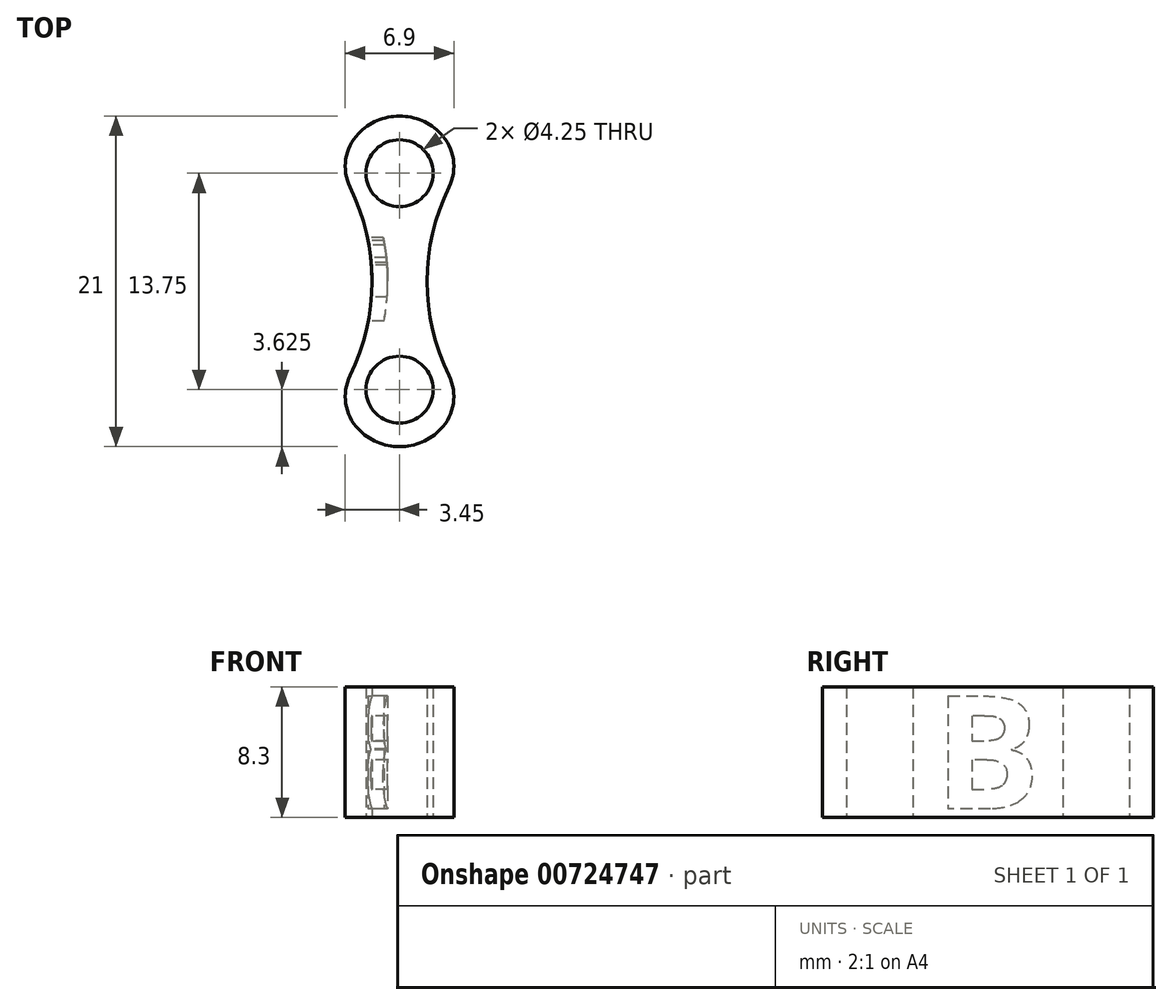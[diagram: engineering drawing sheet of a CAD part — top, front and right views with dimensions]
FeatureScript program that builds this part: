
annotation { "Feature Type Name" : "Feature", "Feature Type Description" : "" }
export const myFeature = defineFeature(function(context is Context, id is Id, definition is map)
    precondition{}
    {
        {
            var Q0;
            Q0=qCreatedBy(makeId("Top.planeOp"),FACE);
            var sketch = newSketch(context, id + "F0", { "sketchPlane" : qUnion([Q0])});
            skLineSegment(sketch, "E0", {"start": v(0, 6.88) * mm, "end": v(0, -6.88) * mm});
            skCircle(sketch, "E1", {"center": v(0, 6.88) * mm, "radius": 2.12 * mm});
            skLineSegment(sketch, "E2", {"start": v(-1.75, 0) * mm, "end": v(1.75, 0) * mm});
            skCircle(sketch, "E3", {"center": v(0, -6.88) * mm, "radius": 2.12 * mm});
            skCircle(sketch, "E4", {"center": v(0, 6.88) * mm, "radius": 3.62 * mm});
            skCircle(sketch, "E5", {"center": v(0, -6.88) * mm, "radius": 3.62 * mm});
            skArc(sketch, "E6", {"start": v(-3.12, -5.03) * mm, "mid": v(-1.75, 0) * mm, "end": v(-3.12, 5.03) * mm});
            skArc(sketch, "E7.MirrorCS", {"start": v(3.12, -5.03) * mm, "mid": v(1.75, 0) * mm, "end": v(3.12, 5.03) * mm});
            skPoint(sketch, "E8.orphan", {"position": v(3.12, 5.03) * mm});
            skPoint(sketch, "E9.orphan", {"position": v(-3.12, 5.03) * mm});
            skPoint(sketch, "E10.orphan", {"position": v(6.24, 6.88) * mm});
            skArc(sketch, "E11", {"start": v(-3.63, -6.87) * mm, "mid": v(-1.75, 0) * mm, "end": v(-3.63, 6.87) * mm});
            skArc(sketch, "E12.MirrorCS", {"start": v(3.63, -6.87) * mm, "mid": v(1.75, 0) * mm, "end": v(3.63, 6.87) * mm});
            skSolve(sketch);
        }
        {
            var Q0;
            Q0=makeQuery(id+"F0.imprint","IMPRINT",FACE,{"disambiguationData":[TD([[makeQuery(id+"F0.imprint","IMPRINT",EDGE,{"derivedFrom":sQuery(id+"F0.wireOp",EDGE,"E1")}),-1.0]])]});
            var Q1;
            {var subQ0=sQuery(id+"F0.wireOp",EDGE,"E4");var subQ1=sQuery(id+"F0.wireOp",EDGE,"E0");var subQ2=makeQuery(id+"F0.imprint","INTERSECT",VERTEX,{"derivedFrom":[subQ1,subQ0]});Q1=makeQuery(id+"F0.imprint","IMPRINT",FACE,{"disambiguationData":[TD([[makeQuery(id+"F0.imprint","IMPRINT",EDGE,{"disambiguationData":[TD([[subQ2,-1.0]])],"derivedFrom":subQ1}),-1.0]])]});}
            var Q2;
            {var subQ0=sQuery(id+"F0.wireOp",EDGE,"E4");var subQ1=sQuery(id+"F0.wireOp",EDGE,"E0");var subQ2=makeQuery(id+"F0.imprint","INTERSECT",VERTEX,{"derivedFrom":[subQ1,subQ0]});Q2=makeQuery(id+"F0.imprint","IMPRINT",FACE,{"disambiguationData":[TD([[makeQuery(id+"F0.imprint","IMPRINT",EDGE,{"disambiguationData":[TD([[subQ2,-1.0]])],"derivedFrom":subQ1}),1.0]])]});}
            var Q3;
            {var subQ0=sQuery(id+"F0.wireOp",EDGE,"E5");var subQ1=sQuery(id+"F0.wireOp",EDGE,"E0");var subQ2=makeQuery(id+"F0.imprint","INTERSECT",VERTEX,{"derivedFrom":[subQ1,subQ0]});Q3=makeQuery(id+"F0.imprint","IMPRINT",FACE,{"disambiguationData":[TD([[makeQuery(id+"F0.imprint","IMPRINT",EDGE,{"disambiguationData":[TD([[subQ2,1.0]])],"derivedFrom":subQ1}),1.0]])]});}
            var Q4;
            {var subQ0=sQuery(id+"F0.wireOp",EDGE,"E5");var subQ1=sQuery(id+"F0.wireOp",EDGE,"E0");var subQ2=makeQuery(id+"F0.imprint","INTERSECT",VERTEX,{"derivedFrom":[subQ1,subQ0]});Q4=makeQuery(id+"F0.imprint","IMPRINT",FACE,{"disambiguationData":[TD([[makeQuery(id+"F0.imprint","IMPRINT",EDGE,{"disambiguationData":[TD([[subQ2,1.0]])],"derivedFrom":subQ1}),-1.0]])]});}
            var Q5;
            Q5=makeQuery(id+"F0.imprint","IMPRINT",FACE,{"disambiguationData":[TD([[makeQuery(id+"F0.imprint","IMPRINT",EDGE,{"derivedFrom":sQuery(id+"F0.wireOp",EDGE,"E3")}),-1.0]])]});
            extrude(context, id + "F1", {"entities" : qUnion([Q0, Q1, Q2, Q3, Q4, Q5]), "depth" : 8.3 * mm, "offsetDistance" : 25 * mm});
        }
        {
            var Q0;
            Q0=makeQuery(id+"F1.opExtrude","CAP_VERTEX",VERTEX,{"disambiguationData":[OSD([sQuery(id+"F0.wireOp",EDGE,"E4"),sQuery(id+"F0.wireOp",EDGE,"E11")])],"isStart":false});
            var Q1;
            Q1=makeQuery(id+"F1.opExtrude","CAP_VERTEX",VERTEX,{"disambiguationData":[OSD([sQuery(id+"F0.wireOp",EDGE,"E4"),sQuery(id+"F0.wireOp",EDGE,"E11")])],"isStart":true});
            var Q2;
            Q2=makeQuery(id+"F1.opExtrude","CAP_VERTEX",VERTEX,{"disambiguationData":[OSD([sQuery(id+"F0.wireOp",EDGE,"E5"),sQuery(id+"F0.wireOp",EDGE,"E11")])],"isStart":true});
            cPlane(context, id + "F2", {"entities" : qUnion([Q0, Q1, Q2]), "cplaneType" : CPlaneType.THREE_POINT, "offset" : 10 * mm, "width" : 150 * mm, "height" : 150 * mm});
        }
        {
            var Q0;
            Q0=qCreatedBy(id+"F2.planeOp",FACE);
            var sketch = newSketch(context, id + "F3", { "sketchPlane" : qUnion([Q0])});
            skLineSegment(sketch, "E13", {"start": v(-1.85, 4.15) * mm, "end": v(1.85, 4.15) * mm});
            skPoint(sketch, "E14", {"position": v(0, 4.15) * mm});
            skSolve(sketch);
        }
        {
            var Q0;
            Q0=qCreatedBy(id+"F2.planeOp",FACE);
            var sketch = newSketch(context, id + "F4", { "sketchPlane" : qUnion([Q0])});
            skText(sketch, "E15", { "text": "B", "fontName": "OpenSans-Bold.ttf"});
            const initialGuessF4  = {"E15": [-0.00343, 0.00054, 1, 0, 0.00723]};
            skSetInitialGuess(sketch, initialGuessF4);
            skSolve(sketch);
        }
        {
            var Q0;
            Q0=makeQuery(id+"F4.imprint","IMPRINT",FACE,{"disambiguationData":[TD([[makeQuery(id+"F4.imprint","IMPRINT",EDGE,{"derivedFrom":sQuery(id+"F4.wireOp",EDGE,"E15.sketch_text.stroke-0")}),-1.0]])]});
            var Q1;
            Q1=makeQuery(id+"F1.opExtrude","SWEPT_FACE",FACE,{"disambiguationData":[OSD([sQuery(id+"F0.wireOp",EDGE,"E11")])]});
            extrude(context, id + "F5", {"entities" : qUnion([Q0]), "operationType" : NewBodyOperationType.REMOVE, "endBound" : BoundingType.UP_TO_SURFACE, "depth" : 25 * mm, "endBoundEntityFace" : qUnion([Q1]), "hasOffset" : true, "offsetDistance" : 1 * mm, "offsetOppositeDirection" : true});
        }
        {
            var Q0;
            Q0=makeQuery(id+"F1.opExtrude","SWEPT_EDGE",EDGE,{"disambiguationData":[OSD([sQuery(id+"F0.wireOp",EDGE,"E4"),sQuery(id+"F0.wireOp",EDGE,"E11")])]});
            var Q1;
            Q1=makeQuery(id+"F1.opExtrude","SWEPT_EDGE",EDGE,{"disambiguationData":[OSD([sQuery(id+"F0.wireOp",EDGE,"E5"),sQuery(id+"F0.wireOp",EDGE,"E11")])]});
            var Q2;
            Q2=makeQuery(id+"F1.opExtrude","SWEPT_EDGE",EDGE,{"disambiguationData":[OSD([sQuery(id+"F0.wireOp",EDGE,"E5"),sQuery(id+"F0.wireOp",EDGE,"E12.MirrorCS")])]});
            var Q3;
            Q3=makeQuery(id+"F1.opExtrude","SWEPT_EDGE",EDGE,{"disambiguationData":[OSD([sQuery(id+"F0.wireOp",EDGE,"E4"),sQuery(id+"F0.wireOp",EDGE,"E12.MirrorCS")])]});
            fillet(context, id + "F6", {"entities" : qUnion([Q0, Q1, Q2, Q3]), "radius" : 3 * mm, "tangentPropagation" : true, "allowEdgeOverflow" : false});
        }
    });
